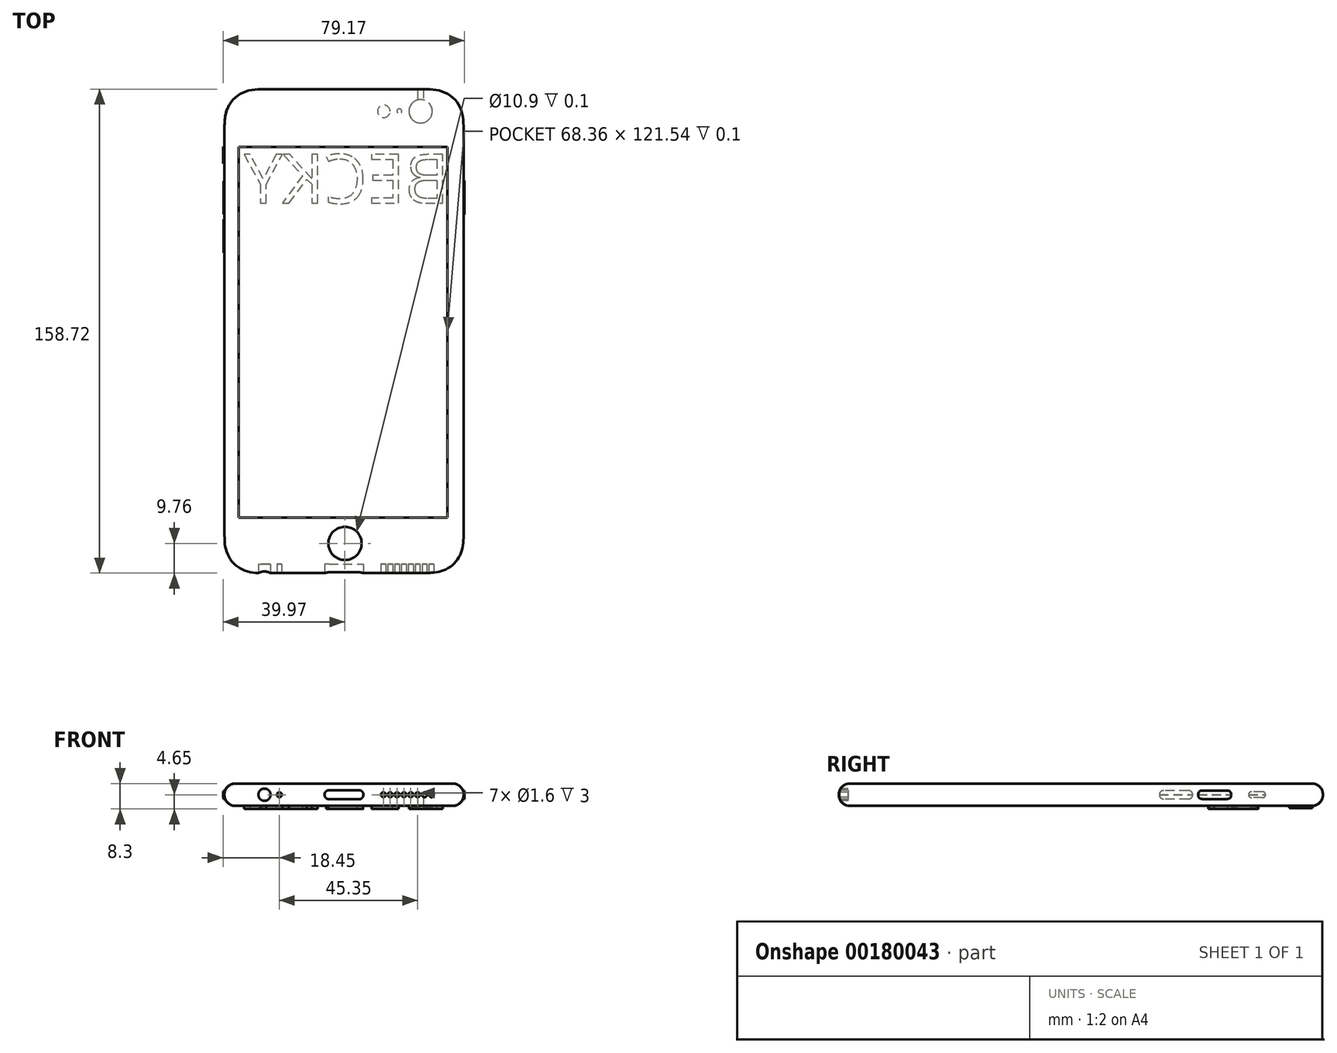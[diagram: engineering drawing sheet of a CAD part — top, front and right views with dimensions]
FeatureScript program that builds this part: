
annotation { "Feature Type Name" : "Feature", "Feature Type Description" : "" }
export const myFeature = defineFeature(function(context is Context, id is Id, definition is map)
    precondition{}
    {
        {
            var Q0;
            Q0=qCreatedBy(makeId("Top.planeOp"),FACE);
            var sketch = newSketch(context, id + "F0", { "sketchPlane" : qUnion([Q0])});
            skLineSegment(sketch, "E0.rect.bottom", {"start": v(25.09, -79.36) * mm, "end": v(-25.09, -79.36) * mm});
            skLineSegment(sketch, "E0.rect.top", {"start": v(25.09, 79.36) * mm, "end": v(-25.09, 79.36) * mm});
            skLineSegment(sketch, "E0.rect.left", {"start": v(39.22, -65.23) * mm, "end": v(39.22, 65.23) * mm});
            skLineSegment(sketch, "E0.rect.right", {"start": v(-39.22, -65.23) * mm, "end": v(-39.22, 65.23) * mm});
            skPoint(sketch, "E0.rect.middle", {"position": v(0, 0) * mm});
            skCircle(sketch, "E1", {"center": v(25.12, 72.09) * mm, "radius": 3.83 * mm});
            skCircle(sketch, "E2", {"center": v(18.16, 72.09) * mm, "radius": 0.8 * mm});
            skCircle(sketch, "E3", {"center": v(13.06, 72.09) * mm, "radius": 2.06 * mm});
            skLineSegment(sketch, "E4", {"start": v(-39.22, 72.1) * mm, "end": v(39.22, 72.1) * mm, "construction": true});
            skPoint(sketch, "E5.visualSharp", {"position": v(-39.22, 79.36) * mm});
            skFitSpline(sketch, "E6", {"points": [v(-25.09, 79.36) * mm, v(-29.02, 79.25) * mm, v(-32.83, 78.38) * mm, v(-36.09, 76.23) * mm, v(-38.24, 72.97) * mm, v(-39.1, 69.16) * mm, v(-39.22, 65.23) * mm], "startDerivative": vector(-8.98, 0) * mm, "endDerivative": vector(0, -8.98) * mm});
            skLineSegment(sketch, "E7", {"start": v(-25.09, 79.36) * mm, "end": v(-39.22, 79.36) * mm, "construction": true});
            skLineSegment(sketch, "E8", {"start": v(-39.22, 79.36) * mm, "end": v(-39.22, 65.23) * mm, "construction": true});
            skLineSegment(sketch, "E9", {"start": v(0, 79.36) * mm, "end": v(0, -79.36) * mm, "construction": true});
            skLineSegment(sketch, "E10", {"start": v(-39.22, 0) * mm, "end": v(39.22, 0) * mm, "construction": true});
            skFitSpline(sketch, "E11.MirrorCS", {"points": [v(25.09, 79.36) * mm, v(29.02, 79.25) * mm, v(32.83, 78.38) * mm, v(36.09, 76.23) * mm, v(38.24, 72.97) * mm, v(39.1, 69.16) * mm, v(39.22, 65.23) * mm], "startDerivative": vector(8.98, 0) * mm, "endDerivative": vector(0, -8.98) * mm});
            skFitSpline(sketch, "E12.MirrorCS", {"points": [v(-25.09, -79.36) * mm, v(-29.02, -79.25) * mm, v(-32.83, -78.38) * mm, v(-36.09, -76.23) * mm, v(-38.24, -72.97) * mm, v(-39.1, -69.16) * mm, v(-39.22, -65.23) * mm], "startDerivative": vector(-8.98, 0) * mm, "endDerivative": vector(0, 8.98) * mm});
            skFitSpline(sketch, "E13.MirrorCS", {"points": [v(25.09, -79.36) * mm, v(29.02, -79.25) * mm, v(32.83, -78.38) * mm, v(36.09, -76.23) * mm, v(38.24, -72.97) * mm, v(39.1, -69.16) * mm, v(39.22, -65.23) * mm], "startDerivative": vector(8.98, 0) * mm, "endDerivative": vector(0, 8.98) * mm});
            skCircle(sketch, "E14", {"center": v(0, 37.36) * mm, "radius": 11 * mm, "construction": true});
            skSolve(sketch);
        }
        {
            var Q0;
            Q0=makeQuery(id+"F0.imprint","IMPRINT",FACE,{"disambiguationData":[TD([[makeQuery(id+"F0.imprint","IMPRINT",EDGE,{"derivedFrom":sQuery(id+"F0.wireOp",EDGE,"E0.rect.bottom")}),-1.0]])]});
            var Q1;
            Q1=makeQuery(id+"F0.imprint","IMPRINT",FACE,{"disambiguationData":[TD([[makeQuery(id+"F0.imprint","IMPRINT",EDGE,{"derivedFrom":sQuery(id+"F0.wireOp",EDGE,"E1")}),1.0]])]});
            var Q2;
            Q2=makeQuery(id+"F0.imprint","IMPRINT",FACE,{"disambiguationData":[TD([[makeQuery(id+"F0.imprint","IMPRINT",EDGE,{"derivedFrom":sQuery(id+"F0.wireOp",EDGE,"E2")}),1.0]])]});
            var Q3;
            Q3=makeQuery(id+"F0.imprint","IMPRINT",FACE,{"disambiguationData":[TD([[makeQuery(id+"F0.imprint","IMPRINT",EDGE,{"derivedFrom":sQuery(id+"F0.wireOp",EDGE,"E3")}),1.0]])]});
            extrude(context, id + "F1", {"entities" : qUnion([Q0, Q1, Q2, Q3]), "depth" : 7.3 * mm});
        }
        {
            var Q0;
            Q0=makeQuery(id+"F0.imprint","IMPRINT",FACE,{"disambiguationData":[TD([[makeQuery(id+"F0.imprint","IMPRINT",EDGE,{"derivedFrom":sQuery(id+"F0.wireOp",EDGE,"E1")}),1.0]])]});
            extrude(context, id + "F2", {"entities" : qUnion([Q0]), "operationType" : NewBodyOperationType.ADD, "oppositeDirection" : true, "depth" : 0.67 * mm});
        }
        {
            var Q0;
            Q0=makeQuery(id+"F0.imprint","IMPRINT",FACE,{"disambiguationData":[TD([[makeQuery(id+"F0.imprint","IMPRINT",EDGE,{"derivedFrom":sQuery(id+"F0.wireOp",EDGE,"E3")}),1.0]])]});
            var Q1;
            Q1=makeQuery(id+"F0.imprint","IMPRINT",FACE,{"disambiguationData":[TD([[makeQuery(id+"F0.imprint","IMPRINT",EDGE,{"derivedFrom":sQuery(id+"F0.wireOp",EDGE,"E2")}),1.0]])]});
            extrude(context, id + "F3", {"entities" : qUnion([Q0, Q1]), "operationType" : NewBodyOperationType.REMOVE, "depth" : 0.1 * mm});
        }
        {
            var Q0;
            Q0=makeQuery(id+"F1.opExtrude","CAP_FACE",FACE,{"disambiguationData":[OSD([sQuery(id+"F0.wireOp",EDGE,"E0.rect.bottom"),sQuery(id+"F0.wireOp",EDGE,"E0.rect.top"),sQuery(id+"F0.wireOp",EDGE,"E0.rect.left"),sQuery(id+"F0.wireOp",EDGE,"E0.rect.right"),sQuery(id+"F0.wireOp",EDGE,"d7852d5b-fe0f-4a90-bdf2-04cff158e1f8.filletArc"),sQuery(id+"F0.wireOp",EDGE,"E5.filletArc"),sQuery(id+"F0.wireOp",EDGE,"7c06d2e9-cdf6-4879-9dee-aab3bc7c6033.filletArc"),sQuery(id+"F0.wireOp",EDGE,"93b3bdb9-dbb8-49f8-8f1e-002f612095da.filletArc")])],"isStart":false});
            var sketch = newSketch(context, id + "F4", { "sketchPlane" : qUnion([Q0])});
            skCircle(sketch, "E15", {"center": v(0.32, -69.6) * mm, "radius": 5.45 * mm});
            skLineSegment(sketch, "E16.bottom", {"start": v(-34.51, 60.44) * mm, "end": v(33.85, 60.44) * mm});
            skLineSegment(sketch, "E16.top", {"start": v(-34.5, -61.1) * mm, "end": v(33.85, -61.1) * mm});
            skLineSegment(sketch, "E16.left", {"start": v(-34.51, 60.44) * mm, "end": v(-34.5, -61.1) * mm});
            skLineSegment(sketch, "E16.right", {"start": v(33.85, 60.44) * mm, "end": v(33.85, -61.1) * mm});
            skSolve(sketch);
        }
        {
            var Q0;
            Q0=makeQuery(id+"F4.imprint","IMPRINT",FACE,{"disambiguationData":[TD([[makeQuery(id+"F4.imprint","IMPRINT",EDGE,{"derivedFrom":sQuery(id+"F4.wireOp",EDGE,"E15")}),1.0]])]});
            extrude(context, id + "F5", {"entities" : qUnion([Q0]), "operationType" : NewBodyOperationType.REMOVE, "oppositeDirection" : true, "depth" : 0.1 * mm});
        }
        {
            var Q0;
            Q0=makeQuery(id+"F4.imprint","IMPRINT",FACE,{"disambiguationData":[TD([[makeQuery(id+"F4.imprint","IMPRINT",EDGE,{"derivedFrom":sQuery(id+"F4.wireOp",EDGE,"E16.bottom")}),-1.0]])]});
            extrude(context, id + "F6", {"entities" : qUnion([Q0]), "operationType" : NewBodyOperationType.REMOVE, "oppositeDirection" : true, "depth" : 0.1 * mm});
        }
        {
            var Q0;
            Q0=makeQuery(id+"F1.opExtrude","SWEPT_FACE",FACE,{"disambiguationData":[OSD([sQuery(id+"F0.wireOp",EDGE,"E0.rect.bottom")])]});
            var sketch = newSketch(context, id + "F7", { "sketchPlane" : qUnion([Q0])});
            skLineSegment(sketch, "E17.0", {"start": v(25.09, 7.3) * mm, "end": v(-25.09, 7.3) * mm, "construction": true});
            skLineSegment(sketch, "E17.1", {"start": v(25.09, 0) * mm, "end": v(-25.09, 0) * mm, "construction": true});
            skLineSegment(sketch, "E17.2", {"start": v(39.22, 7.3) * mm, "end": v(39.22, 0) * mm, "construction": true});
            skLineSegment(sketch, "E17.3", {"start": v(-39.22, 7.3) * mm, "end": v(-39.22, 0) * mm, "construction": true});
            skFitSpline(sketch, "E17.4", {"points": [v(-24.74, 7.3) * mm, v(-29.45, 7.3) * mm, v(-34.16, 7.3) * mm, v(-38.87, 7.3) * mm], "construction": true});
            skFitSpline(sketch, "E17.5", {"points": [v(-24.74, 0) * mm, v(-29.45, 0) * mm, v(-34.16, 0) * mm, v(-38.87, 0) * mm], "construction": true});
            skFitSpline(sketch, "E17.6", {"points": [v(24.74, 0) * mm, v(29.45, 0) * mm, v(34.16, 0) * mm, v(38.87, 0) * mm], "construction": true});
            skFitSpline(sketch, "E17.7", {"points": [v(24.74, 7.3) * mm, v(29.45, 7.3) * mm, v(34.16, 7.3) * mm, v(38.87, 7.3) * mm], "construction": true});
            skLineSegment(sketch, "E18", {"start": v(0, 7.3) * mm, "end": v(0, 0) * mm, "construction": true});
            skLineSegment(sketch, "E19", {"start": v(-39.22, 3.65) * mm, "end": v(-6.4, 3.65) * mm, "construction": true});
            skLineSegment(sketch, "E20", {"start": v(-4.92, 5.12) * mm, "end": v(4.92, 5.12) * mm});
            skLineSegment(sketch, "E21", {"start": v(-4.92, 2.17) * mm, "end": v(4.92, 2.17) * mm});
            skLineSegment(sketch, "E22", {"start": v(-6.4, 3.65) * mm, "end": v(39.22, 3.65) * mm, "construction": true});
            skArc(sketch, "E23", {"start": v(-4.92, 5.13) * mm, "mid": v(-6.4, 3.65) * mm, "end": v(-4.92, 2.17) * mm});
            skArc(sketch, "E24", {"start": v(-4.92, 2.17) * mm, "mid": v(-3.44, 3.65) * mm, "end": v(-4.92, 5.13) * mm, "construction": true});
            skArc(sketch, "E25", {"start": v(4.92, 5.13) * mm, "mid": v(5.96, 4.7) * mm, "end": v(6.4, 3.65) * mm});
            skArc(sketch, "E26", {"start": v(4.92, 2.17) * mm, "mid": v(3.44, 3.65) * mm, "end": v(4.92, 5.13) * mm, "construction": true});
            skArc(sketch, "E27", {"start": v(6.4, 3.65) * mm, "mid": v(5.96, 2.6) * mm, "end": v(4.92, 2.17) * mm});
            skCircle(sketch, "E28", {"center": v(-26.09, 3.65) * mm, "radius": 2 * mm});
            skCircle(sketch, "E29", {"center": v(-21.2, 3.65) * mm, "radius": 0.8 * mm});
            skCircle(sketch, "E30", {"center": v(12.9, 3.65) * mm, "radius": 0.8 * mm});
            skCircle(sketch, "E31.1.0.0", {"center": v(15.15, 3.65) * mm, "radius": 0.8 * mm});
            skCircle(sketch, "E31.2.0.0", {"center": v(17.4, 3.65) * mm, "radius": 0.8 * mm});
            skCircle(sketch, "E31.3.0.0", {"center": v(19.65, 3.65) * mm, "radius": 0.8 * mm});
            skCircle(sketch, "E31.4.0.0", {"center": v(21.9, 3.65) * mm, "radius": 0.8 * mm});
            skCircle(sketch, "E31.5.0.0", {"center": v(24.15, 3.65) * mm, "radius": 0.8 * mm});
            skCircle(sketch, "E31.6.0.0", {"center": v(26.4, 3.65) * mm, "radius": 0.8 * mm});
            skCircle(sketch, "E31.7.0.0", {"center": v(28.65, 3.65) * mm, "radius": 0.8 * mm});
            skLineSegment(sketch, "E31.direction1", {"start": v(12.9, 3.65) * mm, "end": v(15.15, 3.65) * mm, "construction": true});
            skPoint(sketch, "E32", {"position": v(12.1, 3.65) * mm});
            skPoint(sketch, "E33", {"position": v(29.45, 3.65) * mm});
            skLineSegment(sketch, "E34.0", {"start": v(-25.09, 7.3) * mm, "end": v(-25.09, 0) * mm, "construction": true});
            skLineSegment(sketch, "E34.1", {"start": v(25.09, 7.3) * mm, "end": v(25.09, 0) * mm, "construction": true});
            skSolve(sketch);
        }
        {
            var Q0;
            Q0=makeQuery(id+"F1.opExtrude","SWEPT_FACE",FACE,{"disambiguationData":[OSD([sQuery(id+"F0.wireOp",EDGE,"E0.rect.left")])]});
            var sketch = newSketch(context, id + "F8", { "sketchPlane" : qUnion([Q0])});
            skLineSegment(sketch, "E35", {"start": v(-65.23, 2.25) * mm, "end": v(65.23, 2.25) * mm, "construction": true});
            skLineSegment(sketch, "E36", {"start": v(8.97, 4.69) * mm, "end": v(22.34, 4.7) * mm});
            skLineSegment(sketch, "E37", {"start": v(8.97, 2.25) * mm, "end": v(22.34, 2.25) * mm});
            skPoint(sketch, "E38", {"position": v(7.75, 3.47) * mm});
            skPoint(sketch, "E39", {"position": v(23.56, 3.47) * mm});
            skLineSegment(sketch, "E40", {"start": v(39.81, 2.25) * mm, "end": v(47.95, 2.25) * mm});
            skLineSegment(sketch, "E41", {"start": v(39.81, 5.05) * mm, "end": v(39.81, 5.05) * mm});
            skLineSegment(sketch, "E42", {"start": v(39.81, 3.65) * mm, "end": v(47.95, 3.65) * mm, "construction": true});
            skLineSegment(sketch, "E43", {"start": v(39.81, 5.05) * mm, "end": v(47.95, 5.05) * mm});
            skArc(sketch, "E44", {"start": v(47.95, 5.05) * mm, "mid": v(46.55, 3.65) * mm, "end": v(47.95, 2.25) * mm, "construction": true});
            skArc(sketch, "E45", {"start": v(47.95, 2.25) * mm, "mid": v(49.35, 3.65) * mm, "end": v(47.95, 5.05) * mm});
            skArc(sketch, "E46", {"start": v(39.81, 2.25) * mm, "mid": v(41.21, 3.65) * mm, "end": v(39.81, 5.05) * mm, "construction": true});
            skArc(sketch, "E47", {"start": v(39.81, 5.05) * mm, "mid": v(38.41, 3.65) * mm, "end": v(39.81, 2.25) * mm});
            skPoint(sketch, "E48", {"position": v(43.88, 3.65) * mm});
            skPoint(sketch, "E49", {"position": v(38.4, 3.65) * mm});
            skArc(sketch, "E50", {"start": v(8.97, 4.7) * mm, "mid": v(7.75, 3.47) * mm, "end": v(8.97, 2.25) * mm});
            skArc(sketch, "E51", {"start": v(8.97, 2.25) * mm, "mid": v(10.2, 3.47) * mm, "end": v(8.97, 4.7) * mm, "construction": true});
            skArc(sketch, "E52", {"start": v(22.34, 4.7) * mm, "mid": v(21.12, 3.47) * mm, "end": v(22.34, 2.25) * mm, "construction": true});
            skArc(sketch, "E53", {"start": v(22.34, 2.25) * mm, "mid": v(23.56, 3.47) * mm, "end": v(22.34, 4.7) * mm});
            skSolve(sketch);
        }
        {
            var Q0;
            Q0=makeQuery(id+"F1.opExtrude","SWEPT_FACE",FACE,{"disambiguationData":[OSD([sQuery(id+"F0.wireOp",EDGE,"E0.rect.right")])]});
            var sketch = newSketch(context, id + "F9", { "sketchPlane" : qUnion([Q0])});
            skLineSegment(sketch, "E54", {"start": v(-65.23, 3.63) * mm, "end": v(65.23, 3.63) * mm, "construction": true});
            skLineSegment(sketch, "E55", {"start": v(-60.58, 3.65) * mm, "end": v(-54.97, 3.65) * mm, "construction": true});
            skLineSegment(sketch, "E56", {"start": v(-59.6, 2.66) * mm, "end": v(-55.95, 2.66) * mm});
            skLineSegment(sketch, "E57", {"start": v(-59.6, 4.63) * mm, "end": v(-55.95, 4.63) * mm});
            skArc(sketch, "E58", {"start": v(-59.6, 2.66) * mm, "mid": v(-58.61, 3.64) * mm, "end": v(-59.6, 4.63) * mm, "construction": true});
            skArc(sketch, "E59", {"start": v(-59.6, 4.63) * mm, "mid": v(-60.58, 3.64) * mm, "end": v(-59.6, 2.66) * mm});
            skArc(sketch, "E60", {"start": v(-55.95, 2.66) * mm, "mid": v(-54.97, 3.65) * mm, "end": v(-55.95, 4.63) * mm});
            skArc(sketch, "E61", {"start": v(-55.95, 4.63) * mm, "mid": v(-56.94, 3.65) * mm, "end": v(-55.95, 2.66) * mm, "construction": true});
            skPoint(sketch, "E62.first.point", {"position": v(-49.28, 3.63) * mm});
            skPoint(sketch, "E62.second.point", {"position": v(-47.88, 2.23) * mm});
            skPoint(sketch, "E62.third.point", {"position": v(-47.88, 5.03) * mm});
            skPoint(sketch, "E63.first.point", {"position": v(-41.14, 3.63) * mm});
            skPoint(sketch, "E63.second.point", {"position": v(-39.74, 2.23) * mm});
            skPoint(sketch, "E63.third.point", {"position": v(-39.74, 5.03) * mm});
            skLineSegment(sketch, "E64", {"start": v(-47.88, 2.23) * mm, "end": v(-39.74, 2.23) * mm});
            skLineSegment(sketch, "E65", {"start": v(-47.88, 5.03) * mm, "end": v(-39.74, 5.03) * mm});
            skArc(sketch, "E66", {"start": v(-47.88, 5.03) * mm, "mid": v(-49.28, 3.63) * mm, "end": v(-47.88, 2.23) * mm});
            skArc(sketch, "E67", {"start": v(-47.88, 2.23) * mm, "mid": v(-46.48, 3.63) * mm, "end": v(-47.88, 5.03) * mm, "construction": true});
            skArc(sketch, "E68", {"start": v(-39.74, 2.23) * mm, "mid": v(-38.34, 3.63) * mm, "end": v(-39.74, 5.03) * mm});
            skArc(sketch, "E69", {"start": v(-39.74, 5.03) * mm, "mid": v(-41.14, 3.63) * mm, "end": v(-39.74, 2.23) * mm, "construction": true});
            skLineSegment(sketch, "E70", {"start": v(-47.88, 3.63) * mm, "end": v(-39.74, 3.63) * mm, "construction": true});
            skPoint(sketch, "E71", {"position": v(-43.81, 3.63) * mm});
            skLineSegment(sketch, "E72", {"start": v(-35.27, 2.23) * mm, "end": v(-27.13, 2.23) * mm});
            skLineSegment(sketch, "E73", {"start": v(-35.27, 5.03) * mm, "end": v(-27.13, 5.03) * mm});
            skPoint(sketch, "E74.third.point", {"position": v(-36.67, 3.63) * mm});
            skPoint(sketch, "E75.third.point", {"position": v(-25.73, 3.63) * mm});
            skLineSegment(sketch, "E76", {"start": v(-27.13, 3.63) * mm, "end": v(-35.27, 3.63) * mm, "construction": true});
            skPoint(sketch, "E77", {"position": v(-31.2, 3.63) * mm});
            skArc(sketch, "E78", {"start": v(-35.27, 2.23) * mm, "mid": v(-33.87, 3.63) * mm, "end": v(-35.27, 5.03) * mm, "construction": true});
            skArc(sketch, "E79", {"start": v(-35.27, 5.03) * mm, "mid": v(-36.67, 3.63) * mm, "end": v(-35.27, 2.23) * mm});
            skArc(sketch, "E80", {"start": v(-27.13, 5.03) * mm, "mid": v(-28.53, 3.63) * mm, "end": v(-27.13, 2.23) * mm, "construction": true});
            skArc(sketch, "E81", {"start": v(-27.13, 2.23) * mm, "mid": v(-25.73, 3.63) * mm, "end": v(-27.13, 5.03) * mm});
            skSolve(sketch);
        }
        {
            var Q0;
            Q0=makeQuery(id+"F1.opExtrude","CAP_EDGE",EDGE,{"disambiguationData":[OSD([sQuery(id+"F0.wireOp",EDGE,"E0.rect.top")])],"isStart":false});
            var Q1;
            Q1=makeQuery(id+"F1.opExtrude","CAP_EDGE",EDGE,{"disambiguationData":[OSD([sQuery(id+"F0.wireOp",EDGE,"E0.rect.top")])],"isStart":true});
            fillet(context, id + "F10", {"entities" : qUnion([Q0, Q1]), "radius" : (7.1 / 2) * mm, "tangentPropagation" : true, "allowEdgeOverflow" : false});
        }
        {
            var Q0;
            {var subQ0=makeQuery(id+"F1.opExtrude","SWEPT_EDGE",EDGE,{"disambiguationData":[OSD([sQuery(id+"F0.wireOp",EDGE,"E0.rect.bottom"),sQuery(id+"F0.wireOp",EDGE,"E12.MirrorCS")])]});var subQ1=sQuery(id+"F7.wireOp",EDGE,"E28");var subQ3=makeQuery(id+"F7.imprint","INTERSECT",VERTEX,{"disambiguationData":[OD(0.0)],"derivedFrom":[subQ0,subQ1]});Q0=makeQuery(id+"F7.imprint","IMPRINT",FACE,{"disambiguationData":[TD([[makeQuery(id+"F7.imprint","IMPRINT",EDGE,{"disambiguationData":[TD([[subQ3,-1.0]])],"derivedFrom":subQ1}),1.0]])]});}
            var Q1;
            Q1=makeQuery(id+"F7.imprint","IMPRINT",FACE,{"disambiguationData":[TD([[makeQuery(id+"F7.imprint","IMPRINT",EDGE,{"derivedFrom":sQuery(id+"F7.wireOp",EDGE,"E29")}),1.0]])]});
            var Q2;
            Q2=makeQuery(id+"F7.imprint","IMPRINT",FACE,{"disambiguationData":[TD([[makeQuery(id+"F7.imprint","IMPRINT",EDGE,{"derivedFrom":sQuery(id+"F7.wireOp",EDGE,"E20")}),-1.0]])]});
            var Q3;
            Q3=makeQuery(id+"F7.imprint","IMPRINT",FACE,{"disambiguationData":[TD([[makeQuery(id+"F7.imprint","IMPRINT",EDGE,{"derivedFrom":sQuery(id+"F7.wireOp",EDGE,"E30")}),1.0]])]});
            var Q4;
            Q4=makeQuery(id+"F7.imprint","IMPRINT",FACE,{"disambiguationData":[TD([[makeQuery(id+"F7.imprint","IMPRINT",EDGE,{"derivedFrom":sQuery(id+"F7.wireOp",EDGE,"E31.1.0.0")}),1.0]])]});
            var Q5;
            Q5=makeQuery(id+"F7.imprint","IMPRINT",FACE,{"disambiguationData":[TD([[makeQuery(id+"F7.imprint","IMPRINT",EDGE,{"derivedFrom":sQuery(id+"F7.wireOp",EDGE,"E31.2.0.0")}),1.0]])]});
            var Q6;
            Q6=makeQuery(id+"F7.imprint","IMPRINT",FACE,{"disambiguationData":[TD([[makeQuery(id+"F7.imprint","IMPRINT",EDGE,{"derivedFrom":sQuery(id+"F7.wireOp",EDGE,"E31.3.0.0")}),1.0]])]});
            var Q7;
            Q7=makeQuery(id+"F7.imprint","IMPRINT",FACE,{"disambiguationData":[TD([[makeQuery(id+"F7.imprint","IMPRINT",EDGE,{"derivedFrom":sQuery(id+"F7.wireOp",EDGE,"E31.4.0.0")}),1.0]])]});
            var Q8;
            Q8=makeQuery(id+"F7.imprint","IMPRINT",FACE,{"disambiguationData":[TD([[makeQuery(id+"F7.imprint","IMPRINT",EDGE,{"derivedFrom":sQuery(id+"F7.wireOp",EDGE,"E31.5.0.0")}),1.0]])]});
            var Q9;
            Q9=makeQuery(id+"F7.imprint","IMPRINT",FACE,{"disambiguationData":[TD([[makeQuery(id+"F7.imprint","IMPRINT",EDGE,{"derivedFrom":sQuery(id+"F7.wireOp",EDGE,"E31.6.0.0")}),1.0]])]});
            var Q10;
            Q10=makeQuery(id+"F7.imprint","IMPRINT",FACE,{"disambiguationData":[TD([[makeQuery(id+"F7.imprint","IMPRINT",EDGE,{"derivedFrom":sQuery(id+"F7.wireOp",EDGE,"E31.7.0.0")}),1.0]])]});
            var Q11;
            {var subQ0=makeQuery(id+"F1.opExtrude","SWEPT_EDGE",EDGE,{"disambiguationData":[OSD([sQuery(id+"F0.wireOp",EDGE,"E0.rect.bottom"),sQuery(id+"F0.wireOp",EDGE,"E12.MirrorCS")])]});var subQ1=sQuery(id+"F7.wireOp",EDGE,"E28");var subQ3=makeQuery(id+"F7.imprint","INTERSECT",VERTEX,{"disambiguationData":[OD(0.0)],"derivedFrom":[subQ0,subQ1]});Q11=makeQuery(id+"F7.imprint","IMPRINT",FACE,{"disambiguationData":[TD([[makeQuery(id+"F7.imprint","IMPRINT",EDGE,{"disambiguationData":[TD([[subQ3,1.0]])],"derivedFrom":subQ1}),1.0]])]});}
            extrude(context, id + "F11", {"entities" : qUnion([Q0, Q1, Q2, Q3, Q4, Q5, Q6, Q7, Q8, Q9, Q10, Q11]), "oppositeDirection" : true, "depth" : 3 * mm, "hasSecondDirection" : true, "secondDirectionOppositeDirection" : false, "secondDirectionDepth" : 1 * mm});
        }
        {
            var Q0;
            Q0=makeQuery(id+"F11.opExtrude","SWEPT_BODY",BODY,{"disambiguationData":[OSD([sQuery(id+"F7.wireOp",EDGE,"E28")])]});
            var Q1;
            Q1=makeQuery(id+"F11.opExtrude","SWEPT_BODY",BODY,{"disambiguationData":[OSD([sQuery(id+"F7.wireOp",EDGE,"E29")])]});
            var Q2;
            Q2=makeQuery(id+"F11.opExtrude","SWEPT_BODY",BODY,{"disambiguationData":[OSD([sQuery(id+"F7.wireOp",EDGE,"E30")])]});
            var Q3;
            Q3=makeQuery(id+"F11.opExtrude","SWEPT_BODY",BODY,{"disambiguationData":[OSD([sQuery(id+"F7.wireOp",EDGE,"E31.1.0.0")])]});
            var Q4;
            Q4=makeQuery(id+"F11.opExtrude","SWEPT_BODY",BODY,{"disambiguationData":[OSD([sQuery(id+"F7.wireOp",EDGE,"E31.2.0.0")])]});
            var Q5;
            Q5=makeQuery(id+"F11.opExtrude","SWEPT_BODY",BODY,{"disambiguationData":[OSD([sQuery(id+"F7.wireOp",EDGE,"E31.3.0.0")])]});
            var Q6;
            Q6=makeQuery(id+"F11.opExtrude","SWEPT_BODY",BODY,{"disambiguationData":[OSD([sQuery(id+"F7.wireOp",EDGE,"E31.4.0.0")])]});
            var Q7;
            Q7=makeQuery(id+"F11.opExtrude","SWEPT_BODY",BODY,{"disambiguationData":[OSD([sQuery(id+"F7.wireOp",EDGE,"E31.5.0.0")])]});
            var Q8;
            Q8=makeQuery(id+"F11.opExtrude","SWEPT_BODY",BODY,{"disambiguationData":[OSD([sQuery(id+"F7.wireOp",EDGE,"E31.6.0.0")])]});
            var Q9;
            Q9=makeQuery(id+"F11.opExtrude","SWEPT_BODY",BODY,{"disambiguationData":[OSD([sQuery(id+"F7.wireOp",EDGE,"E31.7.0.0")])]});
            var Q10;
            Q10=makeQuery(id+"F11.opExtrude","SWEPT_BODY",BODY,{"disambiguationData":[OSD([sQuery(id+"F7.wireOp",EDGE,"E20"),sQuery(id+"F7.wireOp",EDGE,"E21"),sQuery(id+"F7.wireOp",EDGE,"E23"),sQuery(id+"F7.wireOp",EDGE,"E25"),sQuery(id+"F7.wireOp",EDGE,"E27")])]});
            var Q11;
            Q11=makeQuery(id+"F1.opExtrude","SWEPT_BODY",BODY,{"disambiguationData":[OSD([sQuery(id+"F0.wireOp",EDGE,"E0.rect.bottom"),sQuery(id+"F0.wireOp",EDGE,"E0.rect.top"),sQuery(id+"F0.wireOp",EDGE,"E0.rect.left"),sQuery(id+"F0.wireOp",EDGE,"E0.rect.right"),sQuery(id+"F0.wireOp",EDGE,"E6"),sQuery(id+"F0.wireOp",EDGE,"E11.MirrorCS"),sQuery(id+"F0.wireOp",EDGE,"E12.MirrorCS"),sQuery(id+"F0.wireOp",EDGE,"E13.MirrorCS")])]});
            booleanBodies(context, id + "F12", {"operationType" : BooleanOperationType.SUBTRACTION, "tools" : qUnion([Q0, Q1, Q2, Q3, Q4, Q5, Q6, Q7, Q8, Q9, Q10]), "targets" : qUnion([Q11])});
        }
        {
            var Q0;
            Q0=makeQuery(id+"F8.imprint","IMPRINT",FACE,{"disambiguationData":[TD([[makeQuery(id+"F8.imprint","IMPRINT",EDGE,{"derivedFrom":sQuery(id+"F8.wireOp",EDGE,"E40")}),1.0]])]});
            extrude(context, id + "F13", {"entities" : qUnion([Q0]), "operationType" : NewBodyOperationType.ADD, "depth" : 0.3 * mm});
        }
        {
            var Q0;
            Q0=makeQuery(id+"F9.imprint","IMPRINT",FACE,{"disambiguationData":[TD([[makeQuery(id+"F9.imprint","IMPRINT",EDGE,{"derivedFrom":sQuery(id+"F9.wireOp",EDGE,"E72")}),1.0]])]});
            var Q1;
            Q1=makeQuery(id+"F9.imprint","IMPRINT",FACE,{"disambiguationData":[TD([[makeQuery(id+"F9.imprint","IMPRINT",EDGE,{"derivedFrom":sQuery(id+"F9.wireOp",EDGE,"E64")}),1.0]])]});
            extrude(context, id + "F14", {"entities" : qUnion([Q0, Q1]), "operationType" : NewBodyOperationType.ADD, "depth" : 0.3 * mm});
        }
        {
            var Q0;
            Q0=makeQuery(id+"F9.imprint","IMPRINT",FACE,{"disambiguationData":[TD([[makeQuery(id+"F9.imprint","IMPRINT",EDGE,{"derivedFrom":sQuery(id+"F9.wireOp",EDGE,"E56")}),1.0]])]});
            extrude(context, id + "F15", {"entities" : qUnion([Q0]), "operationType" : NewBodyOperationType.ADD, "depth" : 0.43 * mm});
        }
        {
            var Q0;
            Q0=makeQuery(id+"F1.opExtrude","CAP_FACE",FACE,{"disambiguationData":[OSD([sQuery(id+"F0.wireOp",EDGE,"E0.rect.bottom"),sQuery(id+"F0.wireOp",EDGE,"E0.rect.top"),sQuery(id+"F0.wireOp",EDGE,"E0.rect.left"),sQuery(id+"F0.wireOp",EDGE,"E0.rect.right"),sQuery(id+"F0.wireOp",EDGE,"E6"),sQuery(id+"F0.wireOp",EDGE,"E11.MirrorCS"),sQuery(id+"F0.wireOp",EDGE,"E12.MirrorCS"),sQuery(id+"F0.wireOp",EDGE,"E13.MirrorCS")])],"isStart":true});
            var sketch = newSketch(context, id + "F16", { "sketchPlane" : qUnion([Q0])});
            skText(sketch, "E82", { "text": "BECKY", "fontName": "OpenSans-Regular.ttf"});
            const initialGuessF16  = {"E82": [0.03456, -0.04196, -1, 0, 0.01611]};
            skSetInitialGuess(sketch, initialGuessF16);
            skSolve(sketch);
        }
        {
            var Q0;
            Q0=qSketchRegion(id+"F16",true);
            extrude(context, id + "F17", {"entities" : qUnion([Q0]), "operationType" : NewBodyOperationType.ADD, "depth" : 1 * mm});
        }
    });
